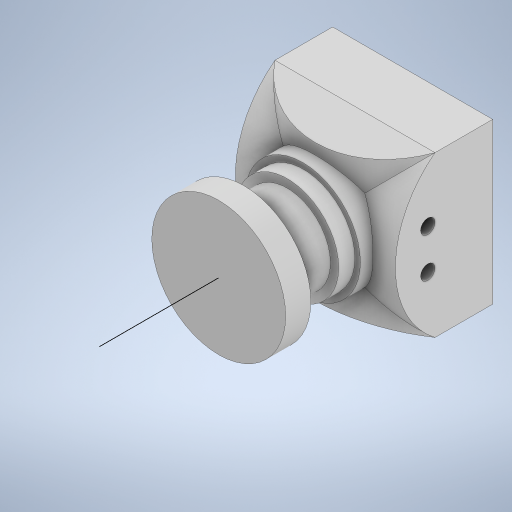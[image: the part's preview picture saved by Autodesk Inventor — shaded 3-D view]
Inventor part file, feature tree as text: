
AUTODESK INVENTOR PART (.ipt)
format: ipt  version: 2023 (Build 270158000, 158)  size: 368,128 bytes
history: native  units: in
note: dims shown in document units (in); Inventor stores cm internally (conversion verified against a paired STEP export)
features: sketch x12, extrude x9, projected_geometry x7, plane x2
ambient origin geometry x8: Origin, YZ Plane, XZ Plane, XY Plane, X Axis, Y Axis, Z Axis, Center Point
bodies: Solid1 (feature_tree)
feature tree (30):
  extrude  "Extrusion1"  Depth=0.874in
  extrude  "Extrusion2"  Depth=0.315in
  sketch  "Sketch3"  dims[d5=0.2854in d6=0.0in d9=0.2165in]
  extrude  "Extrusion4"  Depth=0.2165in
  extrude  "Extrusion5"  Depth=0.0886in
  extrude  "Extrusion6"  Depth=0.374in
  extrude  "Extrusion8"  Depth=0.0886in TaperAngle=0.0deg
  extrude  "Extrusion9"  Depth=0.2362in TaperAngle=0.0deg
  extrude  "Extrusion10"  Depth=0.1378in TaperAngle=0.0deg
  sketch  "Sketch12"  dims[d41=0.4409in]
  plane  "Work Plane2"
  extrude  "Extrusion12"  Depth=0.0394in
  plane  "Work Plane4"
  sketch  "Sketch18"  dims[d49=0.1083in d50=0.0787in d52=0.1083in d53=0.0787in d54=0.0in d55=0.0in d56=-0.437in]
  sketch  "Sketch1"  dims[d0=0.874in d1=0.874in]
  sketch  "Sketch2"  dims[d2=0.315in d3=0.0in d4=0.6299in]
  projected_geometry  "Projected Loop1"
  sketch  "Sketch5"  dims[d10=0.0886in d11=0.0in d12=0.2165in]
  projected_geometry  "Projected Loop3"
  sketch  "Sketch6"  dims[d13=0.0886in d14=0.0in d15=0.374in]
  projected_geometry  "Projected Loop4"
  sketch  "Sketch7"  dims[d16=0.0886in d17=0.0in d23=0.0886in d24=0.0in]
  projected_geometry  "Projected Loop5"
  sketch  "Sketch9"  dims[d25=0.0787in d26=0.2362in d27=0.0in]
  projected_geometry  "Projected Loop8"
  sketch  "Sketch10"  dims[d28=0.7307in d29=0.1378in d30=0.0in]
  projected_geometry  "Projected Loop9"
  sketch  "Sketch11"  dims[d31=1.063in d36=0.0394in]
  sketch  "Sketch17"  dims[d48=0.3543in]
  projected_geometry  "Projected Loop11"
